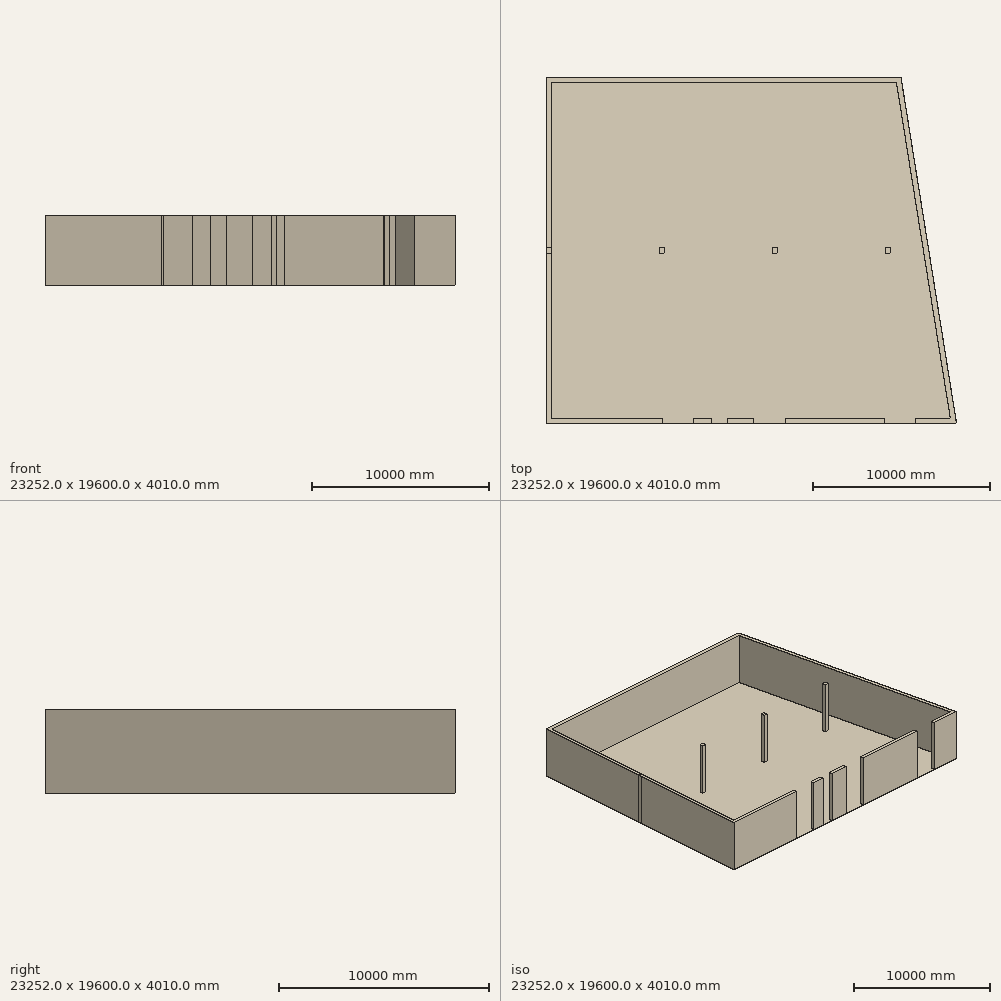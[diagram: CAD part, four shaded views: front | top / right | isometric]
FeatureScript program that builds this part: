
annotation { "Feature Type Name" : "Feature", "Feature Type Description" : "" }
export const myFeature = defineFeature(function(context is Context, id is Id, definition is map)
    precondition{}
    {
        {
            var Q0;
            Q0=qCreatedBy(makeId("Top.planeOp"),FACE);
            var sketch = newSketch(context, id + "F0", { "sketchPlane" : qUnion([Q0])});
            skLineSegment(sketch, "E0.bottom", {"start": v(0, 0) * mm, "end": v(30000, 0) * mm, "construction": true});
            skLineSegment(sketch, "E0.top", {"start": v(0, 30000) * mm, "end": v(30000, 30000) * mm, "construction": true});
            skLineSegment(sketch, "E0.left", {"start": v(0, 0) * mm, "end": v(0, 30000) * mm, "construction": true});
            skLineSegment(sketch, "E0.right", {"start": v(30000, 0) * mm, "end": v(30000, 30000) * mm, "construction": true});
            skLineSegment(sketch, "E1.bottom", {"start": v(0, 0) * mm, "end": v(500, 0) * mm, "construction": true});
            skLineSegment(sketch, "E1.top", {"start": v(0, 500) * mm, "end": v(500, 500) * mm, "construction": true});
            skLineSegment(sketch, "E1.left", {"start": v(0, 0) * mm, "end": v(0, 500) * mm, "construction": true});
            skLineSegment(sketch, "E1.right", {"start": v(500, 0) * mm, "end": v(500, 500) * mm, "construction": true});
            skPoint(sketch, "E2", {"position": v(500, 500) * mm});
            skSolve(sketch);
        }
        {
            var Q0;
            Q0=qCreatedBy(makeId("Top.planeOp"),FACE);
            var sketch = newSketch(context, id + "F1", { "sketchPlane" : qUnion([Q0])});
            skLineSegment(sketch, "E3.bottom", {"start": v(500, 500) * mm, "end": v(20050, 500) * mm});
            skLineSegment(sketch, "E3.top", {"start": v(500, 19500) * mm, "end": v(20050, 19500) * mm});
            skLineSegment(sketch, "E3.left", {"start": v(500, 500) * mm, "end": v(500, 19500) * mm});
            skLineSegment(sketch, "E3.right", {"start": v(20050, 500) * mm, "end": v(20050, 19500) * mm, "construction": true});
            skLineSegment(sketch, "E4", {"start": v(500, 500) * mm, "end": v(23100, 500) * mm});
            skLineSegment(sketch, "E5", {"start": v(23100, 500) * mm, "end": v(20050, 19500) * mm});
            skLineSegment(sketch, "E6.0", {"start": v(200, 19800) * mm, "end": v(20305.68, 19800) * mm});
            skLineSegment(sketch, "E6.1", {"start": v(200, 200) * mm, "end": v(200, 19800) * mm});
            skLineSegment(sketch, "E6.2", {"start": v(200, 200) * mm, "end": v(23452, 200) * mm});
            skLineSegment(sketch, "E6.3", {"start": v(23452, 200) * mm, "end": v(20305.68, 19800) * mm});
            skLineSegment(sketch, "E7.bottom", {"start": v(500, 9850) * mm, "end": v(200, 9850) * mm});
            skLineSegment(sketch, "E7.top", {"start": v(500, 10150) * mm, "end": v(200, 10150) * mm});
            skLineSegment(sketch, "E7.left", {"start": v(500, 9850) * mm, "end": v(500, 10150) * mm});
            skLineSegment(sketch, "E7.right", {"start": v(200, 9850) * mm, "end": v(200, 10150) * mm});
            skPoint(sketch, "E7.middle", {"position": v(350, 10000) * mm});
            skLineSegment(sketch, "E8.bottom", {"start": v(6600, 10150) * mm, "end": v(6900, 10150) * mm});
            skLineSegment(sketch, "E8.top", {"start": v(6600, 9850) * mm, "end": v(6900, 9850) * mm});
            skLineSegment(sketch, "E8.left", {"start": v(6600, 10150) * mm, "end": v(6600, 9850) * mm});
            skLineSegment(sketch, "E8.right", {"start": v(6900, 10150) * mm, "end": v(6900, 9850) * mm});
            skPoint(sketch, "E8.middle", {"position": v(6750, 10000) * mm});
            skLineSegment(sketch, "E9.bottom", {"start": v(13000, 10150) * mm, "end": v(13300, 10150) * mm});
            skLineSegment(sketch, "E9.top", {"start": v(13000, 9850) * mm, "end": v(13300, 9850) * mm});
            skLineSegment(sketch, "E9.left", {"start": v(13000, 10150) * mm, "end": v(13000, 9850) * mm});
            skLineSegment(sketch, "E9.right", {"start": v(13300, 10150) * mm, "end": v(13300, 9850) * mm});
            skPoint(sketch, "E9.middle", {"position": v(13150, 10000) * mm});
            skLineSegment(sketch, "E10", {"start": v(200, -2668.42) * mm, "end": v(500, -2668.42) * mm, "construction": true});
            skLineSegment(sketch, "E11.bottom", {"start": v(19400, 10150) * mm, "end": v(19700, 10150) * mm});
            skLineSegment(sketch, "E11.top", {"start": v(19400, 9850) * mm, "end": v(19700, 9850) * mm});
            skLineSegment(sketch, "E11.left", {"start": v(19400, 10150) * mm, "end": v(19400, 9850) * mm});
            skLineSegment(sketch, "E11.right", {"start": v(19700, 10150) * mm, "end": v(19700, 9850) * mm});
            skPoint(sketch, "E11.middle", {"position": v(19550, 10000) * mm});
            skPoint(sketch, "E12", {"position": v(350, -2668.42) * mm});
            skLineSegment(sketch, "E13", {"start": v(-557.87, 19800) * mm, "end": v(-557.87, 19500) * mm, "construction": true});
            skPoint(sketch, "E14", {"position": v(-557.87, 19650) * mm});
            skPoint(sketch, "E15", {"position": v(6750, 19650) * mm});
            skLineSegment(sketch, "E16", {"start": v(-789.01, 500) * mm, "end": v(-789.01, 200) * mm, "construction": true});
            skPoint(sketch, "E17", {"position": v(-789.01, 350) * mm});
            skPoint(sketch, "E18", {"position": v(-1656.37, 10000) * mm});
            skPoint(sketch, "E19", {"position": v(200, 10000) * mm});
            skLineSegment(sketch, "E20.bottom", {"start": v(8550, 500) * mm, "end": v(6750, 500) * mm});
            skLineSegment(sketch, "E20.top", {"start": v(8550, 200) * mm, "end": v(6750, 200) * mm});
            skLineSegment(sketch, "E20.left", {"start": v(8550, 500) * mm, "end": v(8550, 200) * mm});
            skLineSegment(sketch, "E20.right", {"start": v(6750, 500) * mm, "end": v(6750, 200) * mm});
            skPoint(sketch, "E20.middle", {"position": v(7650, 350) * mm});
            skLineSegment(sketch, "E21.bottom", {"start": v(10450, 500) * mm, "end": v(9550, 500) * mm});
            skLineSegment(sketch, "E21.top", {"start": v(10450, 200) * mm, "end": v(9550, 200) * mm});
            skLineSegment(sketch, "E21.left", {"start": v(10450, 500) * mm, "end": v(10450, 200) * mm});
            skLineSegment(sketch, "E21.right", {"start": v(9550, 500) * mm, "end": v(9550, 200) * mm});
            skPoint(sketch, "E21.middle", {"position": v(10000, 350) * mm});
            skLineSegment(sketch, "E22.bottom", {"start": v(13750, 500) * mm, "end": v(11950, 500) * mm});
            skLineSegment(sketch, "E22.top", {"start": v(13750, 200) * mm, "end": v(11950, 200) * mm});
            skLineSegment(sketch, "E22.left", {"start": v(13750, 500) * mm, "end": v(13750, 200) * mm});
            skLineSegment(sketch, "E22.right", {"start": v(11950, 500) * mm, "end": v(11950, 200) * mm});
            skPoint(sketch, "E22.middle", {"position": v(12850, 350) * mm});
            skLineSegment(sketch, "E23.bottom", {"start": v(21150, 500) * mm, "end": v(19350, 500) * mm});
            skLineSegment(sketch, "E23.top", {"start": v(21150, 200) * mm, "end": v(19350, 200) * mm});
            skLineSegment(sketch, "E23.left", {"start": v(21150, 500) * mm, "end": v(21150, 200) * mm});
            skLineSegment(sketch, "E23.right", {"start": v(19350, 500) * mm, "end": v(19350, 200) * mm});
            skPoint(sketch, "E23.middle", {"position": v(20250, 350) * mm});
            skPoint(sketch, "E23.middle.positionSnap0", {"position": v(13750, 350) * mm});
            skPoint(sketch, "E23.centerSnap0", {"position": v(13750, 350) * mm});
            skSolve(sketch);
        }
        {
            var Q0;
            Q0 = qSketchRegion(id + "F1", true);
            var Q1;
            {var subQ3=sQuery(id+"F1.wireOp",EDGE,"E3.top");Q1=makeQuery(id+"F1.imprint","IMPRINT",FACE,{"disambiguationData":[TD([[makeQuery(id+"F1.imprint","IMPRINT",EDGE,{"derivedFrom":subQ3}),-1.0]])]});}
            var Q2;
            Q2=makeQuery(id+"F1.imprint","IMPRINT",FACE,{"disambiguationData":[TD([[makeQuery(id+"F1.imprint","IMPRINT",EDGE,{"derivedFrom":sQuery(id+"F1.wireOp",EDGE,"E8.bottom")}),-1.0]])]});
            var Q3;
            Q3=makeQuery(id+"F1.imprint","IMPRINT",FACE,{"disambiguationData":[TD([[makeQuery(id+"F1.imprint","IMPRINT",EDGE,{"derivedFrom":sQuery(id+"F1.wireOp",EDGE,"E9.bottom")}),-1.0]])]});
            var Q4;
            Q4=makeQuery(id+"F1.imprint","IMPRINT",FACE,{"disambiguationData":[TD([[makeQuery(id+"F1.imprint","IMPRINT",EDGE,{"derivedFrom":sQuery(id+"F1.wireOp",EDGE,"E11.bottom")}),-1.0]])]});
            extrude(context, id + "F2", {"entities" : qUnion([Q0, Q1, Q2, Q3, Q4]), "oppositeDirection" : true, "depth" : 10 * mm});
        }
        {
            var Q0;
            {var subQ7=sQuery(id+"F1.wireOp",EDGE,"E3.top");Q0=makeQuery(id+"F1.imprint","IMPRINT",FACE,{"disambiguationData":[TD([[makeQuery(id+"F1.imprint","IMPRINT",EDGE,{"derivedFrom":subQ7}),1.0]])]});}
            var Q1;
            Q1=makeQuery(id+"F1.imprint","IMPRINT",FACE,{"disambiguationData":[TD([[makeQuery(id+"F1.imprint","IMPRINT",EDGE,{"derivedFrom":sQuery(id+"F1.wireOp",EDGE,"E8.bottom")}),-1.0]])]});
            var Q2;
            Q2=makeQuery(id+"F1.imprint","IMPRINT",FACE,{"disambiguationData":[TD([[makeQuery(id+"F1.imprint","IMPRINT",EDGE,{"derivedFrom":sQuery(id+"F1.wireOp",EDGE,"E9.bottom")}),-1.0]])]});
            var Q3;
            Q3=makeQuery(id+"F1.imprint","IMPRINT",FACE,{"disambiguationData":[TD([[makeQuery(id+"F1.imprint","IMPRINT",EDGE,{"derivedFrom":sQuery(id+"F1.wireOp",EDGE,"E11.bottom")}),-1.0]])]});
            var Q4;
            {var subQ4=sQuery(id+"F1.wireOp",EDGE,"E7.bottom");Q4=makeQuery(id+"F1.imprint","IMPRINT",FACE,{"disambiguationData":[TD([[makeQuery(id+"F1.imprint","IMPRINT",EDGE,{"derivedFrom":subQ4}),1.0]])]});}
            var Q5;
            {var subQ0=sQuery(id+"F1.wireOp",EDGE,"E21.left");Q5=makeQuery(id+"F1.imprint","IMPRINT",FACE,{"disambiguationData":[TD([[makeQuery(id+"F1.imprint","IMPRINT",EDGE,{"derivedFrom":subQ0}),1.0]])]});}
            var Q6;
            {var subQ0=sQuery(id+"F1.wireOp",EDGE,"E20.left");Q6=makeQuery(id+"F1.imprint","IMPRINT",FACE,{"disambiguationData":[TD([[makeQuery(id+"F1.imprint","IMPRINT",EDGE,{"derivedFrom":subQ0}),1.0]])]});}
            var Q7;
            {var subQ0=sQuery(id+"F1.wireOp",EDGE,"E22.left");Q7=makeQuery(id+"F1.imprint","IMPRINT",FACE,{"disambiguationData":[TD([[makeQuery(id+"F1.imprint","IMPRINT",EDGE,{"derivedFrom":subQ0}),1.0]])]});}
            extrude(context, id + "F3", {"entities" : qUnion([Q0, Q1, Q2, Q3, Q4, Q5, Q6, Q7]), "depth" : 4000 * mm});
        }
        {
            var Q0;
            Q0=makeQuery(id+"F1.imprint","IMPRINT",FACE,{"disambiguationData":[TD([[makeQuery(id+"F1.imprint","IMPRINT",EDGE,{"derivedFrom":sQuery(id+"F1.wireOp",EDGE,"E7.bottom")}),-1.0]])]});
            var Q1;
            Q1=makeQuery(id+"F3.opExtrude","CAP_FACE",FACE,{"disambiguationData":[OSD([sQuery(id+"F1.wireOp",EDGE,"E3.top"),sQuery(id+"F1.wireOp",EDGE,"E3.left"),sQuery(id+"F1.wireOp",EDGE,"E4"),sQuery(id+"F1.wireOp",EDGE,"E5"),sQuery(id+"F1.wireOp",EDGE,"E6.0"),sQuery(id+"F1.wireOp",EDGE,"E6.1"),sQuery(id+"F1.wireOp",EDGE,"E6.2"),sQuery(id+"F1.wireOp",EDGE,"E6.3"),sQuery(id+"F1.wireOp",EDGE,"E7.top"),sQuery(id+"F1.wireOp",EDGE,"E22.left")])],"isStart":false});
            extrude(context, id + "F4", {"entities" : qUnion([Q0]), "endBound" : BoundingType.UP_TO_SURFACE, "endBoundEntityFace" : qUnion([Q1]), "depth" : 25 * mm});
        }
    });
